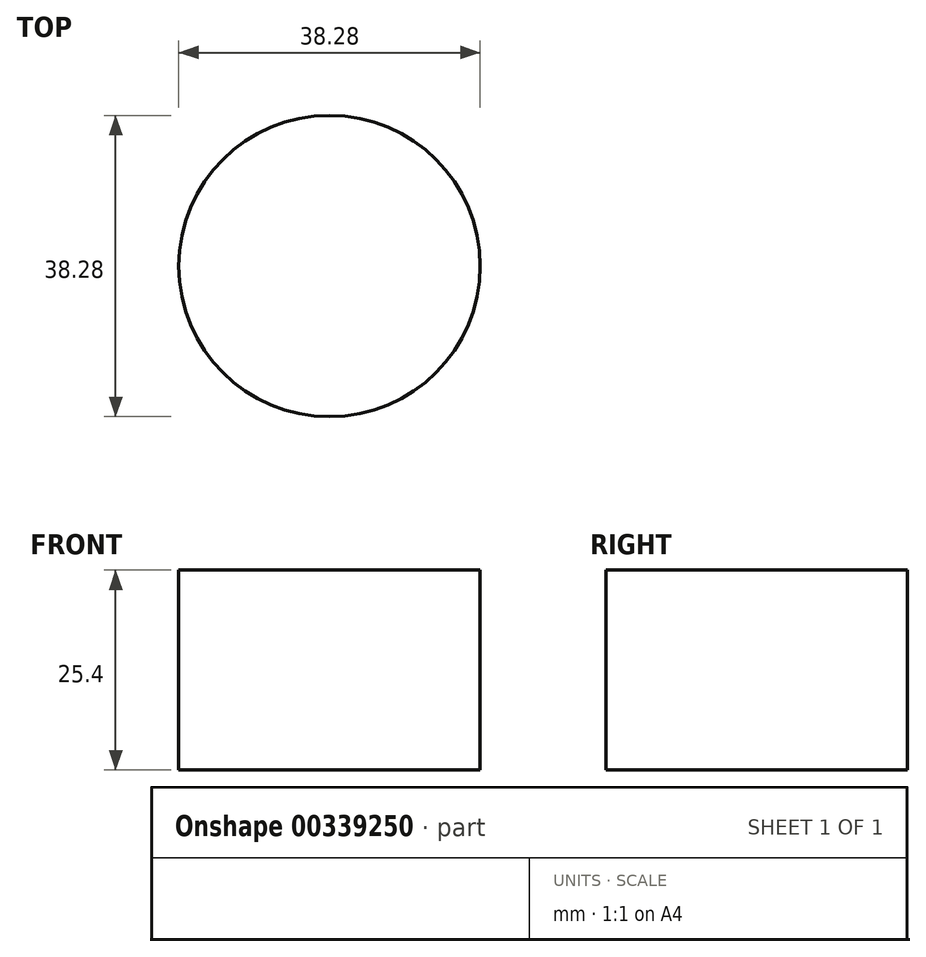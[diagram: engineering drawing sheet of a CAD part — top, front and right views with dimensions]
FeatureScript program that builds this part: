
annotation { "Feature Type Name" : "Feature", "Feature Type Description" : "" }
export const myFeature = defineFeature(function(context is Context, id is Id, definition is map)
    precondition{}
    {
        {
            var Q0;
            Q0=qCreatedBy(makeId("Top.planeOp"),FACE);
            var sketch = newSketch(context, id + "F0", { "sketchPlane" : qUnion([Q0])});
            skLineSegment(sketch, "E0.bottom", {"start": v(-110.88, -13.33) * mm, "end": v(12, -13.33) * mm});
            skLineSegment(sketch, "E0.top", {"start": v(-110.88, 55.98) * mm, "end": v(12, 55.98) * mm});
            skLineSegment(sketch, "E0.left", {"start": v(-110.88, -13.33) * mm, "end": v(-110.88, 55.98) * mm});
            skLineSegment(sketch, "E0.right", {"start": v(12, -13.33) * mm, "end": v(12, 55.98) * mm});
            skLineSegment(sketch, "E1.bottom", {"start": v(-40.27, -18.62) * mm, "end": v(-5.8, -18.62) * mm});
            skLineSegment(sketch, "E1.top", {"start": v(-40.27, -51.48) * mm, "end": v(-5.8, -51.48) * mm});
            skLineSegment(sketch, "E1.left", {"start": v(-40.27, -18.62) * mm, "end": v(-40.27, -51.48) * mm});
            skLineSegment(sketch, "E1.right", {"start": v(-5.8, -18.62) * mm, "end": v(-5.8, -51.48) * mm});
            skCircle(sketch, "E2", {"center": v(37.18, 11.57) * mm, "radius": 19.14 * mm});
            skSolve(sketch);
        }
        {
            var Q0;
            Q0=sQuery(id+"F0.wireOp",EDGE,"E2");
            extrude(context, id + "F1", {"bodyType" : ToolBodyType.SURFACE, "surfaceEntities" : qUnion([Q0]), "depth" : 25.4 * mm, "offsetDistance" : 25.4 * mm});
        }
    });
